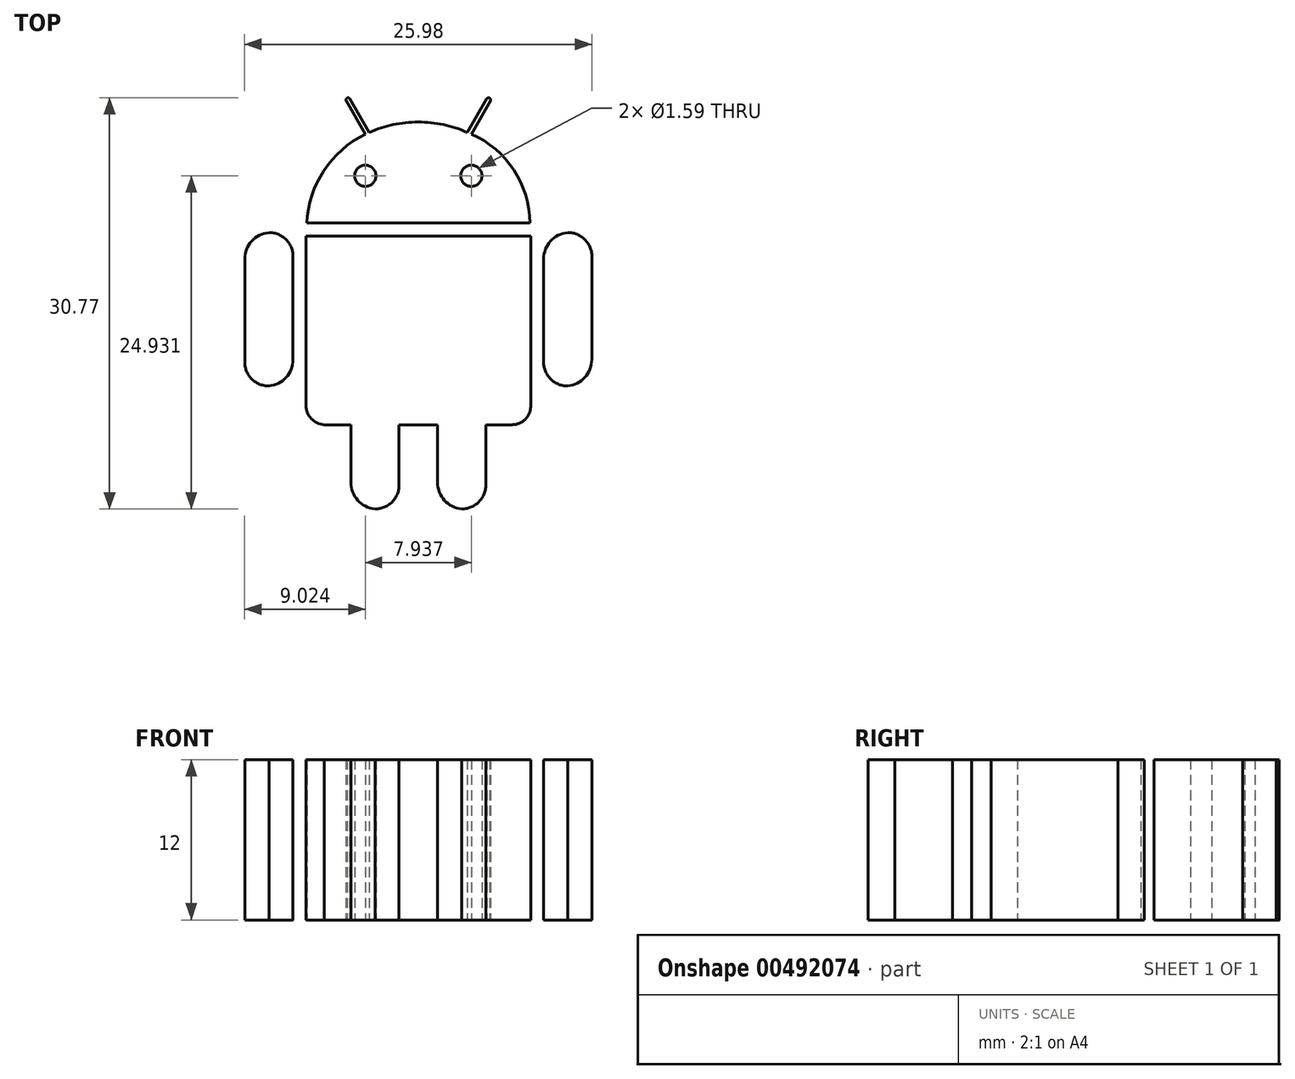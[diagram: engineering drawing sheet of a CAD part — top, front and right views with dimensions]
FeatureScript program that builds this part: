
annotation { "Feature Type Name" : "Feature", "Feature Type Description" : "" }
export const myFeature = defineFeature(function(context is Context, id is Id, definition is map)
    precondition{}
    {
        {
            var Q0;
            Q0=qCreatedBy(makeId("Top.planeOp"),FACE);
            var sketch = newSketch(context, id + "F0", { "sketchPlane" : qUnion([Q0])});
            skArc(sketch, "E0", {"start": v(10.26, 6.15) * mm, "mid": v(8.98, 5.5) * mm, "end": v(8.47, 4.17) * mm});
            skLineSegment(sketch, "E1", {"start": v(8.47, 4.17) * mm, "end": v(8.47, -3.34) * mm});
            skArc(sketch, "E2", {"start": v(8.47, -3.34) * mm, "mid": v(8.92, -4.74) * mm, "end": v(10.26, -5.33) * mm});
            skArc(sketch, "E3", {"start": v(10.26, -5.33) * mm, "mid": v(11.55, -4.69) * mm, "end": v(12.06, -3.34) * mm});
            skLineSegment(sketch, "E4", {"start": v(12.06, -3.34) * mm, "end": v(12.06, 4.17) * mm});
            skArc(sketch, "E5", {"start": v(12.06, 4.17) * mm, "mid": v(11.6, 5.56) * mm, "end": v(10.26, 6.15) * mm});
            skArc(sketch, "E6", {"start": v(-12.1, 6.15) * mm, "mid": v(-13.38, 5.5) * mm, "end": v(-13.9, 4.17) * mm});
            skLineSegment(sketch, "E7", {"start": v(-13.9, 4.17) * mm, "end": v(-13.9, -3.34) * mm});
            skArc(sketch, "E8", {"start": v(-13.9, -3.34) * mm, "mid": v(-13.44, -4.74) * mm, "end": v(-12.1, -5.33) * mm});
            skArc(sketch, "E9", {"start": v(-12.1, -5.33) * mm, "mid": v(-10.81, -4.69) * mm, "end": v(-10.3, -3.34) * mm});
            skLineSegment(sketch, "E10", {"start": v(-10.3, -3.34) * mm, "end": v(-10.3, 4.17) * mm});
            skArc(sketch, "E11", {"start": v(-10.3, 4.17) * mm, "mid": v(-10.75, 5.56) * mm, "end": v(-12.1, 6.15) * mm});
            skLineSegment(sketch, "E12", {"start": v(-9.33, 5.89) * mm, "end": v(-9.33, -6.77) * mm});
            skArc(sketch, "E13", {"start": v(-9.33, -6.77) * mm, "mid": v(-8.93, -7.78) * mm, "end": v(-7.94, -8.22) * mm});
            skLineSegment(sketch, "E14", {"start": v(-7.94, -8.22) * mm, "end": v(-5.96, -8.22) * mm});
            skLineSegment(sketch, "E15", {"start": v(-5.96, -8.22) * mm, "end": v(-5.96, -12.54) * mm});
            skArc(sketch, "E16", {"start": v(-5.96, -12.54) * mm, "mid": v(-5.44, -13.88) * mm, "end": v(-4.16, -14.53) * mm});
            skArc(sketch, "E17", {"start": v(-4.16, -14.53) * mm, "mid": v(-2.82, -13.94) * mm, "end": v(-2.36, -12.54) * mm});
            skLineSegment(sketch, "E18", {"start": v(-2.36, -12.54) * mm, "end": v(-2.36, -8.22) * mm});
            skLineSegment(sketch, "E19", {"start": v(-2.36, -8.22) * mm, "end": v(0.53, -8.22) * mm});
            skLineSegment(sketch, "E20", {"start": v(0.53, -8.22) * mm, "end": v(0.53, -12.54) * mm});
            skArc(sketch, "E21", {"start": v(0.53, -12.54) * mm, "mid": v(1.04, -13.88) * mm, "end": v(2.32, -14.53) * mm});
            skArc(sketch, "E22", {"start": v(2.32, -14.53) * mm, "mid": v(3.67, -13.94) * mm, "end": v(4.13, -12.54) * mm});
            skLineSegment(sketch, "E23", {"start": v(4.13, -12.54) * mm, "end": v(4.13, -8.22) * mm});
            skLineSegment(sketch, "E24", {"start": v(4.13, -8.22) * mm, "end": v(6.1, -8.22) * mm});
            skArc(sketch, "E25", {"start": v(6.1, -8.22) * mm, "mid": v(7.1, -7.8) * mm, "end": v(7.5, -6.77) * mm});
            skLineSegment(sketch, "E26", {"start": v(7.5, -6.77) * mm, "end": v(7.5, 5.89) * mm});
            skLineSegment(sketch, "E27", {"start": v(7.5, 5.89) * mm, "end": v(-9.33, 5.89) * mm});
            skLineSegment(sketch, "E28", {"start": v(-6.32, 16) * mm, "end": v(-4.89, 13.52) * mm});
            skArc(sketch, "E29", {"start": v(-4.89, 13.52) * mm, "mid": v(-7.98, 10.79) * mm, "end": v(-9.26, 6.86) * mm});
            skLineSegment(sketch, "E30", {"start": v(-9.26, 6.86) * mm, "end": v(-0.92, 6.86) * mm});
            skLineSegment(sketch, "E31", {"start": v(-0.92, 6.86) * mm, "end": v(7.43, 6.86) * mm});
            skArc(sketch, "E32", {"start": v(7.43, 6.86) * mm, "mid": v(6.24, 10.84) * mm, "end": v(3.05, 13.52) * mm});
            skLineSegment(sketch, "E33", {"start": v(3.05, 13.52) * mm, "end": v(4.48, 16) * mm});
            skArc(sketch, "E34", {"start": v(4.48, 16) * mm, "mid": v(4.5, 16.12) * mm, "end": v(4.42, 16.22) * mm});
            skArc(sketch, "E35", {"start": v(4.42, 16.22) * mm, "mid": v(4.3, 16.23) * mm, "end": v(4.2, 16.16) * mm});
            skLineSegment(sketch, "E36", {"start": v(4.2, 16.16) * mm, "end": v(2.75, 13.65) * mm});
            skArc(sketch, "E37", {"start": v(2.75, 13.65) * mm, "mid": v(0.96, 14.23) * mm, "end": v(-0.92, 14.42) * mm});
            skArc(sketch, "E38", {"start": v(-0.92, 14.42) * mm, "mid": v(-2.8, 14.23) * mm, "end": v(-4.59, 13.65) * mm});
            skLineSegment(sketch, "E39", {"start": v(-4.59, 13.65) * mm, "end": v(-6.04, 16.16) * mm});
            skArc(sketch, "E40", {"start": v(-6.04, 16.16) * mm, "mid": v(-6.14, 16.23) * mm, "end": v(-6.25, 16.22) * mm});
            skArc(sketch, "E41", {"start": v(-6.25, 16.22) * mm, "mid": v(-6.32, 16.12) * mm, "end": v(-6.32, 16) * mm});
            skLineSegment(sketch, "E42", {"start": v(-6.32, 16) * mm, "end": v(-6.32, 16) * mm});
            skLineSegment(sketch, "E43", {"start": v(-40, 40) * mm, "end": v(-40, -40) * mm});
            skLineSegment(sketch, "E44", {"start": v(-40, -40) * mm, "end": v(40, -40) * mm});
            skLineSegment(sketch, "E45", {"start": v(40, -40) * mm, "end": v(40, 40) * mm});
            skLineSegment(sketch, "E46", {"start": v(40, 40) * mm, "end": v(-40, 40) * mm});
            skCircle(sketch, "E47", {"center": v(-4.89, 10.4) * mm, "radius": 0.8 * mm});
            skCircle(sketch, "E48", {"center": v(3.05, 10.4) * mm, "radius": 0.8 * mm});
            skSolve(sketch);
        }
        {
            var Q0;
            Q0=makeQuery(id+"F0.imprint","IMPRINT",FACE,{"disambiguationData":[TD([[makeQuery(id+"F0.imprint","IMPRINT",EDGE,{"derivedFrom":sQuery(id+"F0.wireOp",EDGE,"E6")}),1.0]])]});
            var Q1;
            Q1=makeQuery(id+"F0.imprint","IMPRINT",FACE,{"disambiguationData":[TD([[makeQuery(id+"F0.imprint","IMPRINT",EDGE,{"derivedFrom":sQuery(id+"F0.wireOp",EDGE,"E0")}),1.0]])]});
            var Q2;
            Q2=makeQuery(id+"F0.imprint","IMPRINT",FACE,{"disambiguationData":[TD([[makeQuery(id+"F0.imprint","IMPRINT",EDGE,{"derivedFrom":sQuery(id+"F0.wireOp",EDGE,"E12")}),1.0]])]});
            var Q3;
            Q3=makeQuery(id+"F0.imprint","IMPRINT",FACE,{"disambiguationData":[TD([[makeQuery(id+"F0.imprint","IMPRINT",EDGE,{"derivedFrom":sQuery(id+"F0.wireOp",EDGE,"E28")}),1.0]])]});
            extrude(context, id + "F1", {"entities" : qUnion([Q0, Q1, Q2, Q3]), "depth" : 12 * mm});
        }
    });
